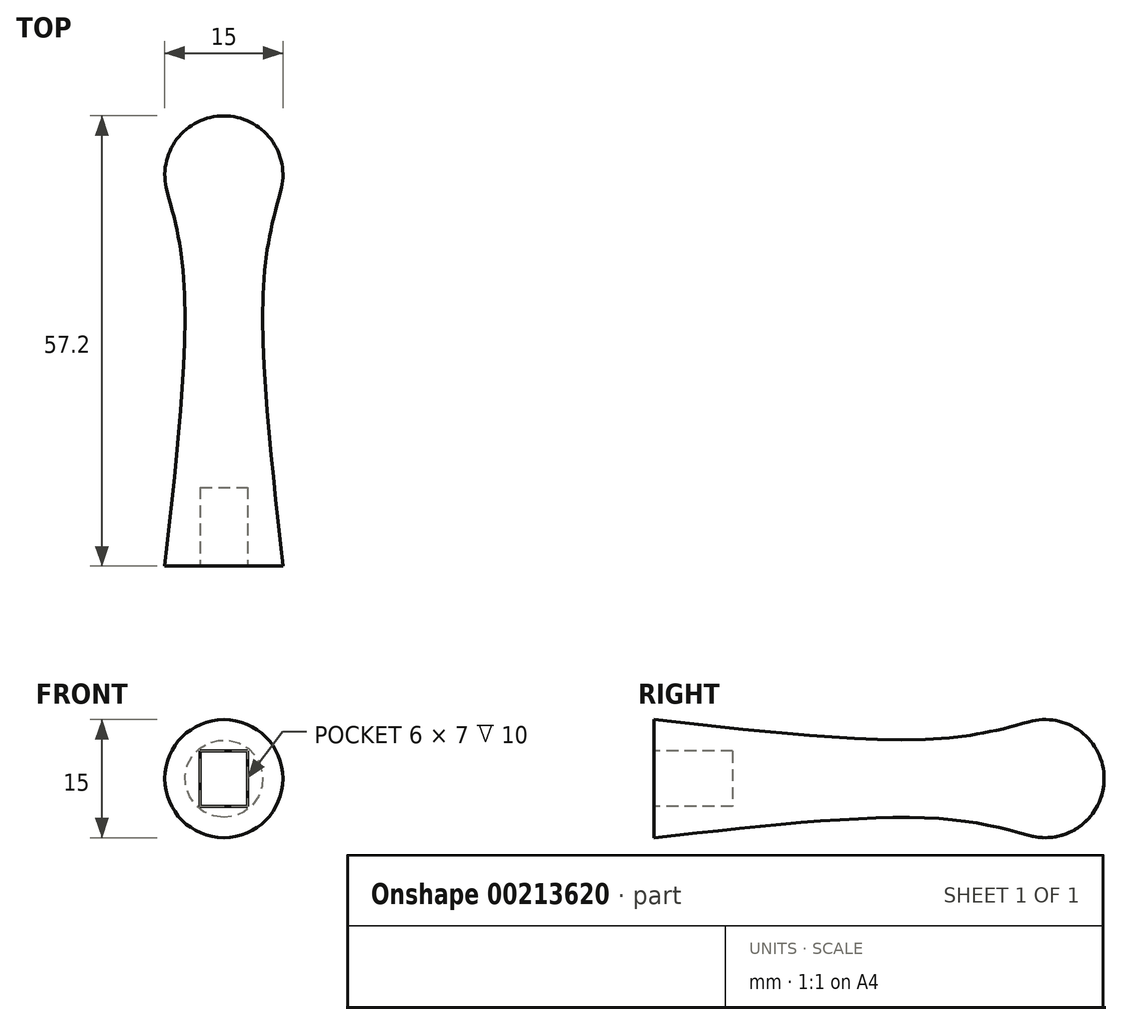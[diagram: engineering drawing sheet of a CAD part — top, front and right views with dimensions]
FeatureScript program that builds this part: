
annotation { "Feature Type Name" : "Feature", "Feature Type Description" : "" }
export const myFeature = defineFeature(function(context is Context, id is Id, definition is map)
    precondition{}
    {
        {
            var Q0;
            Q0=qCreatedBy(makeId("Right.planeOp"),FACE);
            var sketch = newSketch(context, id + "F0", { "sketchPlane" : qUnion([Q0])});
            skLineSegment(sketch, "E0", {"start": v(0, 0) * mm, "end": v(57.2, 0) * mm});
            skLineSegment(sketch, "E1", {"start": v(0, 0) * mm, "end": v(0, 7.5) * mm});
            skLineSegment(sketch, "E2", {"start": v(0, 7.5) * mm, "end": v(49.7, 7.5) * mm});
            skLineSegment(sketch, "E3", {"start": v(49.7, 7.5) * mm, "end": v(49.7, 0) * mm});
            skArc(sketch, "E4", {"start": v(57.2, 0) * mm, "mid": v(49.7, 7.5) * mm, "end": v(42.2, 0) * mm});
            skPoint(sketch, "E5", {"position": v(35, 5) * mm});
            skFitSpline(sketch, "E6", {"points": [v(0, 7.5) * mm, v(35, 5) * mm, v(47.66, 7.22) * mm], "startDerivative": vector(63.06, -6.93) * mm, "endDerivative": vector(28.52, 8.06) * mm});
            skSolve(sketch);
        }
        {
            var Q0;
            {var subQ0=sQuery(id+"F0.wireOp",EDGE,"E1");Q0=makeQuery(id+"F0.imprint","IMPRINT",FACE,{"disambiguationData":[TD([[makeQuery(id+"F0.imprint","IMPRINT",EDGE,{"derivedFrom":subQ0}),-1.0]])]});}
            var Q1;
            {var subQ0=sQuery(id+"F0.wireOp",EDGE,"E3");Q1=makeQuery(id+"F0.imprint","IMPRINT",FACE,{"disambiguationData":[TD([[makeQuery(id+"F0.imprint","IMPRINT",EDGE,{"derivedFrom":subQ0}),-1.0]])]});}
            var Q2;
            {var subQ3=sQuery(id+"F0.wireOp",EDGE,"E3");Q2=makeQuery(id+"F0.imprint","IMPRINT",FACE,{"disambiguationData":[TD([[makeQuery(id+"F0.imprint","IMPRINT",EDGE,{"derivedFrom":subQ3}),1.0]])]});}
            var Q3;
            Q3=sQuery(id+"F0.wireOp",EDGE,"E0");
            revolve(context, id + "F1", {"entities" : qUnion([Q0, Q1, Q2]), "axis" : qUnion([Q3]), "revolveType" : RevolveType.FULL});
        }
        {
            var Q0;
            Q0=makeQuery(id+"F1.opRevolve","SWEPT_FACE",FACE,{"disambiguationData":[OSD([sQuery(id+"F0.wireOp",EDGE,"E1")])]});
            var sketch = newSketch(context, id + "F2", { "sketchPlane" : qUnion([Q0])});
            skLineSegment(sketch, "E7.bottom", {"start": v(-3, 3.5) * mm, "end": v(3, 3.5) * mm});
            skLineSegment(sketch, "E7.top", {"start": v(-3, -3.5) * mm, "end": v(3, -3.5) * mm});
            skLineSegment(sketch, "E7.left", {"start": v(-3, 3.5) * mm, "end": v(-3, -3.5) * mm});
            skLineSegment(sketch, "E7.right", {"start": v(3, 3.5) * mm, "end": v(3, -3.5) * mm});
            skPoint(sketch, "E7.middle", {"position": v(0, 0) * mm});
            skSolve(sketch);
        }
        {
            var Q0;
            Q0 = qSketchRegion(id + "F2", true);
            extrude(context, id + "F3", {"entities" : qUnion([Q0]), "operationType" : NewBodyOperationType.REMOVE, "oppositeDirection" : true, "depth" : 10 * mm});
        }
    });
